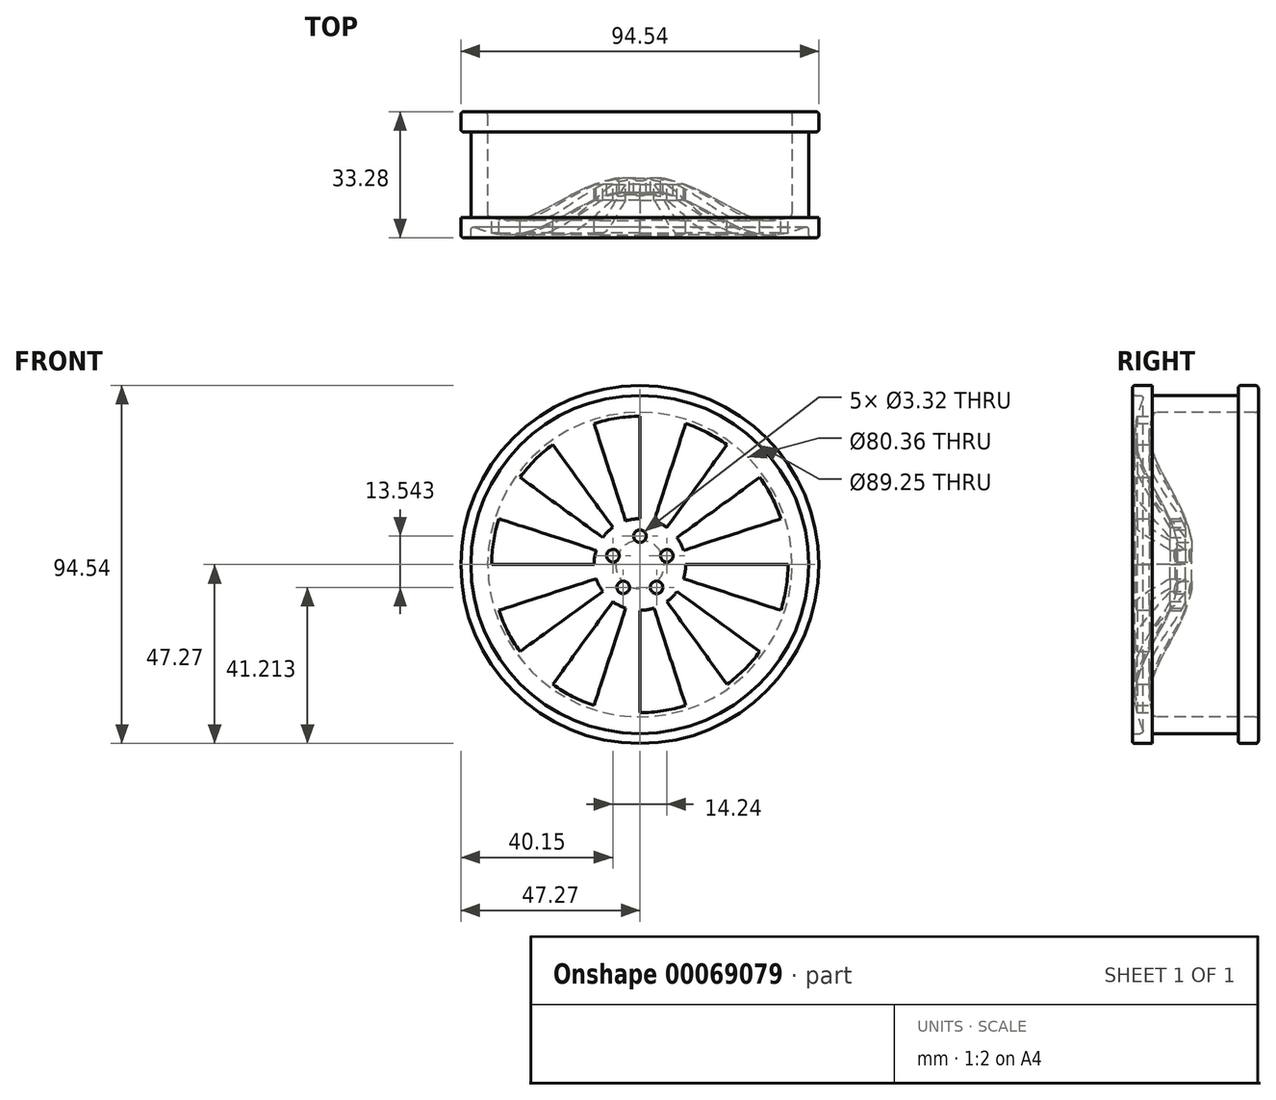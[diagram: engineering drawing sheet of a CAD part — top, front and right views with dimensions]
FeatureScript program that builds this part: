
annotation { "Feature Type Name" : "Feature", "Feature Type Description" : "" }
export const myFeature = defineFeature(function(context is Context, id is Id, definition is map)
    precondition{}
    {
        {
            var Q0;
            Q0=qCreatedBy(makeId("Top.planeOp"),FACE);
            var sketch = newSketch(context, id + "F0", { "sketchPlane" : qUnion([Q0])});
            skLineSegment(sketch, "E0.top", {"start": v(40.18, 30.1) * mm, "end": v(44.63, 30.1) * mm});
            skLineSegment(sketch, "E0.right", {"start": v(44.63, 2.16) * mm, "end": v(44.63, 27.94) * mm});
            skLineSegment(sketch, "E1.bottom", {"start": v(44.63, 30.1) * mm, "end": v(47.27, 30.1) * mm});
            skLineSegment(sketch, "E1.top", {"start": v(44.63, 0) * mm, "end": v(47.27, 0) * mm});
            skLineSegment(sketch, "E1.left", {"start": v(44.63, 27.94) * mm, "end": v(44.63, 2.16) * mm});
            skLineSegment(sketch, "E1.right", {"start": v(47.27, 30.1) * mm, "end": v(47.27, 27.94) * mm});
            skLineSegment(sketch, "E2.0", {"start": v(44.63, 2.16) * mm, "end": v(47.27, 2.16) * mm});
            skLineSegment(sketch, "E3.0", {"start": v(44.63, 27.94) * mm, "end": v(47.27, 27.94) * mm});
            skLineSegment(sketch, "E4.trimOffspring", {"start": v(47.27, 2.16) * mm, "end": v(47.27, 0) * mm});
            skLineSegment(sketch, "E5.0", {"start": v(40.18, 30.1) * mm, "end": v(40.18, 2.58) * mm});
            skLineSegment(sketch, "E6.bottom", {"start": v(0, 8.72) * mm, "end": v(6.4, 8.72) * mm});
            skLineSegment(sketch, "E6.top", {"start": v(0, 12.54) * mm, "end": v(6.4, 12.54) * mm});
            skLineSegment(sketch, "E6.left", {"start": v(0, 8.72) * mm, "end": v(0, 12.54) * mm});
            skPoint(sketch, "E7.1.internal.orphan", {"position": v(3.96, 8.72) * mm});
            skFitSpline(sketch, "E8", {"points": [v(6.4, 8.72) * mm, v(14.11, 5.82) * mm, v(31.92, -2.22) * mm, v(44.63, 0) * mm], "startDerivative": vector(25.8, -7.53) * mm, "endDerivative": vector(36.1, 13.86) * mm});
            skFitSpline(sketch, "E9", {"points": [v(6.4, 12.54) * mm, v(15.53, 9.4) * mm, v(32.03, 1.58) * mm, v(40.18, 2.58) * mm], "startDerivative": vector(27.2, -6.9) * mm, "endDerivative": vector(26.25, 9) * mm});
            skSolve(sketch);
        }
        {
            var Q0;
            Q0=makeQuery(id+"F0.imprint","IMPRINT",FACE,{"disambiguationData":[TD([[makeQuery(id+"F0.imprint","IMPRINT",EDGE,{"derivedFrom":sQuery(id+"F0.wireOp",EDGE,"E0.top")}),-1.0]])]});
            var Q1;
            Q1=sQuery(id+"F0.wireOp",EDGE,"E6.left");
            revolve(context, id + "F1", {"entities" : qUnion([Q0]), "axis" : qUnion([Q1]), "revolveType" : RevolveType.FULL});
        }
        {
            var Q0;
            Q0=makeQuery(id+"F1.opRevolve","SWEPT_FACE",FACE,{"disambiguationData":[OSD([sQuery(id+"F0.wireOp",EDGE,"E0.top"),sQuery(id+"F0.wireOp",EDGE,"E1.bottom")])]});
            var sketch = newSketch(context, id + "F2", { "sketchPlane" : qUnion([Q0])});
            skArc(sketch, "E10", {"start": v(-3.74, 11.52) * mm, "mid": v(-5.5, 10.79) * mm, "end": v(-7.12, 9.8) * mm});
            skLineSegment(sketch, "E11", {"start": v(-39.11, 0) * mm, "end": v(-12.1, 0) * mm});
            skLineSegment(sketch, "E12", {"start": v(0, 39.11) * mm, "end": v(0, 12.1) * mm});
            skLineSegment(sketch, "E13.1.0", {"start": v(-37.2, 12.09) * mm, "end": v(-11.52, 3.74) * mm});
            skLineSegment(sketch, "E13.1.1", {"start": v(-12.09, -37.2) * mm, "end": v(-3.74, -11.52) * mm});
            skLineSegment(sketch, "E13.2.0", {"start": v(-22.99, -31.64) * mm, "end": v(-7.12, -9.8) * mm});
            skLineSegment(sketch, "E13.2.1", {"start": v(31.64, -22.99) * mm, "end": v(9.8, -7.12) * mm});
            skLineSegment(sketch, "E13.3.0", {"start": v(22.99, -31.64) * mm, "end": v(7.12, -9.8) * mm});
            skLineSegment(sketch, "E13.3.1", {"start": v(31.64, 22.99) * mm, "end": v(9.8, 7.12) * mm});
            skLineSegment(sketch, "E13.4.0", {"start": v(37.2, 12.09) * mm, "end": v(11.52, 3.74) * mm});
            skLineSegment(sketch, "E13.4.1", {"start": v(-12.09, 37.2) * mm, "end": v(-3.74, 11.52) * mm});
            skArc(sketch, "E14", {"start": v(-12.09, 37.2) * mm, "mid": v(-17.76, 34.85) * mm, "end": v(-22.99, 31.64) * mm});
            skArc(sketch, "E15.trimOffspring", {"start": v(12.09, 37.2) * mm, "mid": v(6.12, 38.63) * mm, "end": v(0, 39.11) * mm});
            skArc(sketch, "E16.trimOffspring", {"start": v(31.64, 22.99) * mm, "mid": v(27.66, 27.66) * mm, "end": v(22.99, 31.64) * mm});
            skArc(sketch, "E17.trimOffspring", {"start": v(39.11, 0) * mm, "mid": v(38.63, 6.12) * mm, "end": v(37.2, 12.09) * mm});
            skArc(sketch, "E18.trimOffspring", {"start": v(31.64, -22.99) * mm, "mid": v(34.85, -17.76) * mm, "end": v(37.2, -12.09) * mm});
            skArc(sketch, "E19.trimOffspring", {"start": v(12.09, -37.2) * mm, "mid": v(17.76, -34.85) * mm, "end": v(22.99, -31.64) * mm});
            skArc(sketch, "E20.trimOffspring", {"start": v(-12.09, -37.2) * mm, "mid": v(-6.12, -38.63) * mm, "end": v(0, -39.11) * mm});
            skArc(sketch, "E21.trimOffspring", {"start": v(-31.64, -22.99) * mm, "mid": v(-27.66, -27.66) * mm, "end": v(-22.99, -31.64) * mm});
            skArc(sketch, "E22.trimOffspring", {"start": v(-39.11, 0) * mm, "mid": v(-38.63, -6.12) * mm, "end": v(-37.2, -12.09) * mm});
            skArc(sketch, "E23.trimOffspring", {"start": v(-31.64, 22.99) * mm, "mid": v(-34.85, 17.76) * mm, "end": v(-37.2, 12.09) * mm});
            skArc(sketch, "E24.trimOffspring", {"start": v(3.74, 11.52) * mm, "mid": v(1.9, 11.96) * mm, "end": v(0, 12.1) * mm});
            skArc(sketch, "E25.trimOffspring", {"start": v(9.8, 7.12) * mm, "mid": v(8.56, 8.56) * mm, "end": v(7.12, 9.8) * mm});
            skArc(sketch, "E26.trimOffspring", {"start": v(12.1, 0) * mm, "mid": v(11.96, 1.9) * mm, "end": v(11.52, 3.74) * mm});
            skArc(sketch, "E27.trimOffspring", {"start": v(9.8, -7.12) * mm, "mid": v(10.79, -5.5) * mm, "end": v(11.52, -3.74) * mm});
            skArc(sketch, "E28.trimOffspring", {"start": v(3.74, -11.52) * mm, "mid": v(5.5, -10.79) * mm, "end": v(7.12, -9.8) * mm});
            skArc(sketch, "E29.trimOffspring", {"start": v(-3.74, -11.52) * mm, "mid": v(-1.9, -11.96) * mm, "end": v(0, -12.1) * mm});
            skArc(sketch, "E30.trimOffspring", {"start": v(-9.8, -7.12) * mm, "mid": v(-8.56, -8.56) * mm, "end": v(-7.12, -9.8) * mm});
            skArc(sketch, "E31.trimOffspring", {"start": v(-12.1, 0) * mm, "mid": v(-11.96, -1.9) * mm, "end": v(-11.52, -3.74) * mm});
            skArc(sketch, "E32.trimOffspring", {"start": v(-9.8, 7.12) * mm, "mid": v(-10.79, 5.5) * mm, "end": v(-11.52, 3.74) * mm});
            skLineSegment(sketch, "E33.trimOffspring", {"start": v(11.52, -3.74) * mm, "end": v(37.2, -12.09) * mm});
            skLineSegment(sketch, "E34.trimOffspring", {"start": v(-9.8, 7.12) * mm, "end": v(-31.64, 22.99) * mm});
            skLineSegment(sketch, "E35.trimOffspring", {"start": v(-7.12, 9.8) * mm, "end": v(-22.99, 31.64) * mm});
            skLineSegment(sketch, "E36.trimOffspring", {"start": v(3.74, -11.52) * mm, "end": v(12.09, -37.2) * mm});
            skLineSegment(sketch, "E37.trimOffspring", {"start": v(0, -12.1) * mm, "end": v(0, -39.11) * mm});
            skLineSegment(sketch, "E38.trimOffspring", {"start": v(3.74, 11.52) * mm, "end": v(12.09, 37.2) * mm});
            skLineSegment(sketch, "E39.trimOffspring", {"start": v(7.12, 9.8) * mm, "end": v(22.99, 31.64) * mm});
            skLineSegment(sketch, "E40.trimOffspring", {"start": v(-9.8, -7.12) * mm, "end": v(-31.64, -22.99) * mm});
            skLineSegment(sketch, "E41.trimOffspring", {"start": v(-11.52, -3.74) * mm, "end": v(-37.2, -12.09) * mm});
            skLineSegment(sketch, "E42.trimOffspring", {"start": v(12.1, 0) * mm, "end": v(39.11, 0) * mm});
            skCircle(sketch, "E43", {"center": v(0, 7.49) * mm, "radius": 1.66 * mm});
            skCircle(sketch, "E44.1.0", {"center": v(-7.12, 2.31) * mm, "radius": 1.66 * mm});
            skCircle(sketch, "E44.2.0", {"center": v(-4.4, -6.06) * mm, "radius": 1.66 * mm});
            skCircle(sketch, "E44.3.0", {"center": v(4.4, -6.06) * mm, "radius": 1.66 * mm});
            skCircle(sketch, "E44.4.0", {"center": v(7.12, 2.31) * mm, "radius": 1.66 * mm});
            skPoint(sketch, "E45.orphan", {"position": v(-38.21, 12.42) * mm});
            skPoint(sketch, "E46.orphan", {"position": v(-32.5, 23.62) * mm});
            skPoint(sketch, "E47.orphan", {"position": v(-23.62, 32.5) * mm});
            skPoint(sketch, "E48.orphan", {"position": v(-40.18, 0) * mm});
            skPoint(sketch, "E49.orphan", {"position": v(-12.42, 38.21) * mm});
            skPoint(sketch, "E50.orphan", {"position": v(0, 40.18) * mm});
            skPoint(sketch, "E51.orphan", {"position": v(12.42, 38.21) * mm});
            skPoint(sketch, "E52.orphan", {"position": v(-38.21, -12.42) * mm});
            skPoint(sketch, "E53.orphan", {"position": v(23.62, 32.5) * mm});
            skPoint(sketch, "E54.orphan", {"position": v(32.5, 23.62) * mm});
            skPoint(sketch, "E55.orphan", {"position": v(38.21, 12.42) * mm});
            skPoint(sketch, "E56.orphan", {"position": v(40.18, 0) * mm});
            skPoint(sketch, "E57.orphan", {"position": v(-32.5, -23.62) * mm});
            skPoint(sketch, "E58.orphan", {"position": v(-23.62, -32.5) * mm});
            skPoint(sketch, "E59.orphan", {"position": v(-12.42, -38.21) * mm});
            skPoint(sketch, "E60.orphan", {"position": v(0, -40.18) * mm});
            skPoint(sketch, "E61.orphan", {"position": v(12.42, -38.21) * mm});
            skPoint(sketch, "E62.orphan", {"position": v(23.62, -32.5) * mm});
            skPoint(sketch, "E63.orphan", {"position": v(32.5, -23.62) * mm});
            skPoint(sketch, "E64.orphan", {"position": v(38.21, -12.42) * mm});
            skSolve(sketch);
        }
        {
            var Q0;
            Q0=makeQuery(id+"F2.imprint","IMPRINT",FACE,{"disambiguationData":[TD([[makeQuery(id+"F2.imprint","IMPRINT",EDGE,{"derivedFrom":sQuery(id+"F2.wireOp",EDGE,"E13.1.0")}),1.0]])]});
            var Q1;
            Q1=makeQuery(id+"F2.imprint","IMPRINT",FACE,{"disambiguationData":[TD([[makeQuery(id+"F2.imprint","IMPRINT",EDGE,{"derivedFrom":sQuery(id+"F2.wireOp",EDGE,"E10")}),-1.0]])]});
            var Q2;
            Q2=makeQuery(id+"F2.imprint","IMPRINT",FACE,{"disambiguationData":[TD([[makeQuery(id+"F2.imprint","IMPRINT",EDGE,{"derivedFrom":sQuery(id+"F2.wireOp",EDGE,"E12")}),1.0]])]});
            var Q3;
            Q3=makeQuery(id+"F2.imprint","IMPRINT",FACE,{"disambiguationData":[TD([[makeQuery(id+"F2.imprint","IMPRINT",EDGE,{"derivedFrom":sQuery(id+"F2.wireOp",EDGE,"E13.3.1")}),-1.0]])]});
            var Q4;
            Q4=makeQuery(id+"F2.imprint","IMPRINT",FACE,{"disambiguationData":[TD([[makeQuery(id+"F2.imprint","IMPRINT",EDGE,{"derivedFrom":sQuery(id+"F2.wireOp",EDGE,"E13.4.0")}),1.0]])]});
            var Q5;
            Q5=makeQuery(id+"F2.imprint","IMPRINT",FACE,{"disambiguationData":[TD([[makeQuery(id+"F2.imprint","IMPRINT",EDGE,{"derivedFrom":sQuery(id+"F2.wireOp",EDGE,"E13.2.1")}),-1.0]])]});
            var Q6;
            Q6=makeQuery(id+"F2.imprint","IMPRINT",FACE,{"disambiguationData":[TD([[makeQuery(id+"F2.imprint","IMPRINT",EDGE,{"derivedFrom":sQuery(id+"F2.wireOp",EDGE,"E13.3.0")}),1.0]])]});
            var Q7;
            Q7=makeQuery(id+"F2.imprint","IMPRINT",FACE,{"disambiguationData":[TD([[makeQuery(id+"F2.imprint","IMPRINT",EDGE,{"derivedFrom":sQuery(id+"F2.wireOp",EDGE,"E13.1.1")}),-1.0]])]});
            var Q8;
            Q8=makeQuery(id+"F2.imprint","IMPRINT",FACE,{"disambiguationData":[TD([[makeQuery(id+"F2.imprint","IMPRINT",EDGE,{"derivedFrom":sQuery(id+"F2.wireOp",EDGE,"E13.2.0")}),1.0]])]});
            var Q9;
            Q9=makeQuery(id+"F2.imprint","IMPRINT",FACE,{"disambiguationData":[TD([[makeQuery(id+"F2.imprint","IMPRINT",EDGE,{"derivedFrom":sQuery(id+"F2.wireOp",EDGE,"E11")}),-1.0]])]});
            var Q10;
            Q10=makeQuery(id+"F2.imprint","IMPRINT",FACE,{"disambiguationData":[TD([[makeQuery(id+"F2.imprint","IMPRINT",EDGE,{"derivedFrom":sQuery(id+"F2.wireOp",EDGE,"E44.1.0")}),1.0]])]});
            var Q11;
            Q11=makeQuery(id+"F2.imprint","IMPRINT",FACE,{"disambiguationData":[TD([[makeQuery(id+"F2.imprint","IMPRINT",EDGE,{"derivedFrom":sQuery(id+"F2.wireOp",EDGE,"E43")}),1.0]])]});
            var Q12;
            Q12=makeQuery(id+"F2.imprint","IMPRINT",FACE,{"disambiguationData":[TD([[makeQuery(id+"F2.imprint","IMPRINT",EDGE,{"derivedFrom":sQuery(id+"F2.wireOp",EDGE,"E44.4.0")}),1.0]])]});
            var Q13;
            Q13=makeQuery(id+"F2.imprint","IMPRINT",FACE,{"disambiguationData":[TD([[makeQuery(id+"F2.imprint","IMPRINT",EDGE,{"derivedFrom":sQuery(id+"F2.wireOp",EDGE,"E44.3.0")}),1.0]])]});
            var Q14;
            Q14=makeQuery(id+"F2.imprint","IMPRINT",FACE,{"disambiguationData":[TD([[makeQuery(id+"F2.imprint","IMPRINT",EDGE,{"derivedFrom":sQuery(id+"F2.wireOp",EDGE,"E44.2.0")}),1.0]])]});
            extrude(context, id + "F3", {"entities" : qUnion([Q0, Q1, Q2, Q3, Q4, Q5, Q6, Q7, Q8, Q9, Q10, Q11, Q12, Q13, Q14]), "operationType" : NewBodyOperationType.REMOVE, "endBound" : BoundingType.THROUGH_ALL, "oppositeDirection" : true, "depth" : 25.4 * mm});
        }
        {
            var Q0;
            Q0=makeQuery(id+"F1.opRevolve","SWEPT_FACE",FACE,{"disambiguationData":[OSD([sQuery(id+"F0.wireOp",EDGE,"E1.top")])]});
            extrude(context, id + "F4", {"entities" : qUnion([Q0]), "operationType" : NewBodyOperationType.ADD, "depth" : 3.17 * mm});
        }
        {
            var Q0;
            Q0=makeQuery(id+"F1.opRevolve","SWEPT_FACE",FACE,{"disambiguationData":[OSD([sQuery(id+"F0.wireOp",EDGE,"E3.0")])]});
            extrude(context, id + "F5", {"entities" : qUnion([Q0]), "operationType" : NewBodyOperationType.ADD, "depth" : 3.17 * mm});
        }
        {
            var Q0;
            Q0=makeQuery(id+"F4.opExtrude","CAP_EDGE",EDGE,{"disambiguationData":[OSD([sQuery(id+"F0.wireOp",EDGE,"E1.top"),sQuery(id+"F0.wireOp",EDGE,"b8091df5-9ebb-4b62-9d2d-79493e6e60fd.trimOffspring")])],"isStart":false});
            var Q1;
            {var subQ0=sQuery(id+"F0.wireOp",EDGE,"b8091df5-9ebb-4b62-9d2d-79493e6e60fd.trimOffspring");var subQ1=sQuery(id+"F0.wireOp",EDGE,"E1.top");Q1=makeQuery(id+"F4.boolean.opBoolean","MERGE",EDGE,{"derivedFrom":[makeQuery(id+"F1.opRevolve","SWEPT_EDGE",EDGE,{"disambiguationData":[OSD([subQ1,subQ0])]}),makeQuery(id+"F4.opExtrude","CAP_EDGE",EDGE,{"disambiguationData":[OSD([subQ1,subQ0])],"isStart":true})]});}
            var Q2;
            Q2=makeQuery(id+"F3.boolean.opBoolean","INTERSECT",EDGE,{"derivedFrom":[makeQuery(id+"F1.opRevolve","SWEPT_FACE",FACE,{"disambiguationData":[OSD([sQuery(id+"F0.wireOp",EDGE,"b8091df5-9ebb-4b62-9d2d-79493e6e60fd.trimOffspring")])]}),makeQuery(id+"F3.opExtrude","SWEPT_FACE",FACE,{"disambiguationData":[OSD([sQuery(id+"F2.wireOp",EDGE,"E19.trimOffspring")])]})]});
            var Q3;
            Q3=makeQuery(id+"F3.boolean.opBoolean","INTERSECT",EDGE,{"derivedFrom":[makeQuery(id+"F1.opRevolve","SWEPT_FACE",FACE,{"disambiguationData":[OSD([sQuery(id+"F0.wireOp",EDGE,"b8091df5-9ebb-4b62-9d2d-79493e6e60fd.trimOffspring")])]}),makeQuery(id+"F3.opExtrude","SWEPT_FACE",FACE,{"disambiguationData":[OSD([sQuery(id+"F2.wireOp",EDGE,"E20.trimOffspring")])]})]});
            var Q4;
            Q4=makeQuery(id+"F3.boolean.opBoolean","INTERSECT",EDGE,{"derivedFrom":[makeQuery(id+"F1.opRevolve","SWEPT_FACE",FACE,{"disambiguationData":[OSD([sQuery(id+"F0.wireOp",EDGE,"b8091df5-9ebb-4b62-9d2d-79493e6e60fd.trimOffspring")])]}),makeQuery(id+"F3.opExtrude","SWEPT_FACE",FACE,{"disambiguationData":[OSD([sQuery(id+"F2.wireOp",EDGE,"E21.trimOffspring")])]})]});
            var Q5;
            Q5=makeQuery(id+"F3.boolean.opBoolean","INTERSECT",EDGE,{"derivedFrom":[makeQuery(id+"F1.opRevolve","SWEPT_FACE",FACE,{"disambiguationData":[OSD([sQuery(id+"F0.wireOp",EDGE,"b8091df5-9ebb-4b62-9d2d-79493e6e60fd.trimOffspring")])]}),makeQuery(id+"F3.opExtrude","SWEPT_FACE",FACE,{"disambiguationData":[OSD([sQuery(id+"F2.wireOp",EDGE,"E22.trimOffspring")])]})]});
            var Q6;
            Q6=makeQuery(id+"F3.boolean.opBoolean","INTERSECT",EDGE,{"derivedFrom":[makeQuery(id+"F1.opRevolve","SWEPT_FACE",FACE,{"disambiguationData":[OSD([sQuery(id+"F0.wireOp",EDGE,"b8091df5-9ebb-4b62-9d2d-79493e6e60fd.trimOffspring")])]}),makeQuery(id+"F3.opExtrude","SWEPT_FACE",FACE,{"disambiguationData":[OSD([sQuery(id+"F2.wireOp",EDGE,"E23.trimOffspring")])]})]});
            var Q7;
            Q7=makeQuery(id+"F3.boolean.opBoolean","INTERSECT",EDGE,{"derivedFrom":[makeQuery(id+"F1.opRevolve","SWEPT_FACE",FACE,{"disambiguationData":[OSD([sQuery(id+"F0.wireOp",EDGE,"b8091df5-9ebb-4b62-9d2d-79493e6e60fd.trimOffspring")])]}),makeQuery(id+"F3.opExtrude","SWEPT_FACE",FACE,{"disambiguationData":[OSD([sQuery(id+"F2.wireOp",EDGE,"E14")])]})]});
            var Q8;
            Q8=makeQuery(id+"F3.boolean.opBoolean","INTERSECT",EDGE,{"derivedFrom":[makeQuery(id+"F1.opRevolve","SWEPT_FACE",FACE,{"disambiguationData":[OSD([sQuery(id+"F0.wireOp",EDGE,"b8091df5-9ebb-4b62-9d2d-79493e6e60fd.trimOffspring")])]}),makeQuery(id+"F3.opExtrude","SWEPT_FACE",FACE,{"disambiguationData":[OSD([sQuery(id+"F2.wireOp",EDGE,"E15.trimOffspring")])]})]});
            var Q9;
            Q9=makeQuery(id+"F3.boolean.opBoolean","INTERSECT",EDGE,{"derivedFrom":[makeQuery(id+"F1.opRevolve","SWEPT_FACE",FACE,{"disambiguationData":[OSD([sQuery(id+"F0.wireOp",EDGE,"b8091df5-9ebb-4b62-9d2d-79493e6e60fd.trimOffspring")])]}),makeQuery(id+"F3.opExtrude","SWEPT_FACE",FACE,{"disambiguationData":[OSD([sQuery(id+"F2.wireOp",EDGE,"E16.trimOffspring")])]})]});
            var Q10;
            Q10=makeQuery(id+"F3.boolean.opBoolean","INTERSECT",EDGE,{"derivedFrom":[makeQuery(id+"F1.opRevolve","SWEPT_FACE",FACE,{"disambiguationData":[OSD([sQuery(id+"F0.wireOp",EDGE,"b8091df5-9ebb-4b62-9d2d-79493e6e60fd.trimOffspring")])]}),makeQuery(id+"F3.opExtrude","SWEPT_FACE",FACE,{"disambiguationData":[OSD([sQuery(id+"F2.wireOp",EDGE,"E17.trimOffspring")])]})]});
            var Q11;
            Q11=makeQuery(id+"F3.boolean.opBoolean","INTERSECT",EDGE,{"derivedFrom":[makeQuery(id+"F1.opRevolve","SWEPT_FACE",FACE,{"disambiguationData":[OSD([sQuery(id+"F0.wireOp",EDGE,"b8091df5-9ebb-4b62-9d2d-79493e6e60fd.trimOffspring")])]}),makeQuery(id+"F3.opExtrude","SWEPT_FACE",FACE,{"disambiguationData":[OSD([sQuery(id+"F2.wireOp",EDGE,"E18.trimOffspring")])]})]});
            var Q12;
            Q12=makeQuery(id+"F3.boolean.opBoolean","INTERSECT",EDGE,{"derivedFrom":[makeQuery(id+"F1.opRevolve","SWEPT_FACE",FACE,{"disambiguationData":[OSD([sQuery(id+"F0.wireOp",EDGE,"b8091df5-9ebb-4b62-9d2d-79493e6e60fd.trimOffspring")])]}),makeQuery(id+"F3.opExtrude","SWEPT_FACE",FACE,{"disambiguationData":[OSD([sQuery(id+"F2.wireOp",EDGE,"E33.trimOffspring")])]})]});
            var Q13;
            Q13=makeQuery(id+"F3.boolean.opBoolean","INTERSECT",EDGE,{"derivedFrom":[makeQuery(id+"F1.opRevolve","SWEPT_FACE",FACE,{"disambiguationData":[OSD([sQuery(id+"F0.wireOp",EDGE,"b8091df5-9ebb-4b62-9d2d-79493e6e60fd.trimOffspring")])]}),makeQuery(id+"F3.opExtrude","SWEPT_FACE",FACE,{"disambiguationData":[OSD([sQuery(id+"F2.wireOp",EDGE,"E13.2.1")])]})]});
            var Q14;
            Q14=makeQuery(id+"F3.boolean.opBoolean","INTERSECT",EDGE,{"derivedFrom":[makeQuery(id+"F1.opRevolve","SWEPT_FACE",FACE,{"disambiguationData":[OSD([sQuery(id+"F0.wireOp",EDGE,"b8091df5-9ebb-4b62-9d2d-79493e6e60fd.trimOffspring")])]}),makeQuery(id+"F3.opExtrude","SWEPT_FACE",FACE,{"disambiguationData":[OSD([sQuery(id+"F2.wireOp",EDGE,"E27.trimOffspring")])]})]});
            var Q15;
            Q15=makeQuery(id+"F3.boolean.opBoolean","INTERSECT",EDGE,{"derivedFrom":[makeQuery(id+"F1.opRevolve","SWEPT_FACE",FACE,{"disambiguationData":[OSD([sQuery(id+"F0.wireOp",EDGE,"b8091df5-9ebb-4b62-9d2d-79493e6e60fd.trimOffspring")])]}),makeQuery(id+"F3.opExtrude","SWEPT_FACE",FACE,{"disambiguationData":[OSD([sQuery(id+"F2.wireOp",EDGE,"E13.3.0")])]})]});
            var Q16;
            Q16=makeQuery(id+"F3.boolean.opBoolean","INTERSECT",EDGE,{"derivedFrom":[makeQuery(id+"F1.opRevolve","SWEPT_FACE",FACE,{"disambiguationData":[OSD([sQuery(id+"F0.wireOp",EDGE,"b8091df5-9ebb-4b62-9d2d-79493e6e60fd.trimOffspring")])]}),makeQuery(id+"F3.opExtrude","SWEPT_FACE",FACE,{"disambiguationData":[OSD([sQuery(id+"F2.wireOp",EDGE,"E36.trimOffspring")])]})]});
            var Q17;
            Q17=makeQuery(id+"F3.boolean.opBoolean","INTERSECT",EDGE,{"derivedFrom":[makeQuery(id+"F1.opRevolve","SWEPT_FACE",FACE,{"disambiguationData":[OSD([sQuery(id+"F0.wireOp",EDGE,"b8091df5-9ebb-4b62-9d2d-79493e6e60fd.trimOffspring")])]}),makeQuery(id+"F3.opExtrude","SWEPT_FACE",FACE,{"disambiguationData":[OSD([sQuery(id+"F2.wireOp",EDGE,"E28.trimOffspring")])]})]});
            var Q18;
            Q18=makeQuery(id+"F3.boolean.opBoolean","INTERSECT",EDGE,{"derivedFrom":[makeQuery(id+"F1.opRevolve","SWEPT_FACE",FACE,{"disambiguationData":[OSD([sQuery(id+"F0.wireOp",EDGE,"b8091df5-9ebb-4b62-9d2d-79493e6e60fd.trimOffspring")])]}),makeQuery(id+"F3.opExtrude","SWEPT_FACE",FACE,{"disambiguationData":[OSD([sQuery(id+"F2.wireOp",EDGE,"E29.trimOffspring")])]})]});
            var Q19;
            Q19=makeQuery(id+"F3.boolean.opBoolean","INTERSECT",EDGE,{"derivedFrom":[makeQuery(id+"F1.opRevolve","SWEPT_FACE",FACE,{"disambiguationData":[OSD([sQuery(id+"F0.wireOp",EDGE,"b8091df5-9ebb-4b62-9d2d-79493e6e60fd.trimOffspring")])]}),makeQuery(id+"F3.opExtrude","SWEPT_FACE",FACE,{"disambiguationData":[OSD([sQuery(id+"F2.wireOp",EDGE,"E37.trimOffspring")])]})]});
            var Q20;
            Q20=makeQuery(id+"F3.boolean.opBoolean","INTERSECT",EDGE,{"derivedFrom":[makeQuery(id+"F1.opRevolve","SWEPT_FACE",FACE,{"disambiguationData":[OSD([sQuery(id+"F0.wireOp",EDGE,"b8091df5-9ebb-4b62-9d2d-79493e6e60fd.trimOffspring")])]}),makeQuery(id+"F3.opExtrude","SWEPT_FACE",FACE,{"disambiguationData":[OSD([sQuery(id+"F2.wireOp",EDGE,"E13.1.1")])]})]});
            var Q21;
            Q21=makeQuery(id+"F3.boolean.opBoolean","INTERSECT",EDGE,{"derivedFrom":[makeQuery(id+"F1.opRevolve","SWEPT_FACE",FACE,{"disambiguationData":[OSD([sQuery(id+"F0.wireOp",EDGE,"b8091df5-9ebb-4b62-9d2d-79493e6e60fd.trimOffspring")])]}),makeQuery(id+"F3.opExtrude","SWEPT_FACE",FACE,{"disambiguationData":[OSD([sQuery(id+"F2.wireOp",EDGE,"E13.2.0")])]})]});
            var Q22;
            Q22=makeQuery(id+"F3.boolean.opBoolean","INTERSECT",EDGE,{"derivedFrom":[makeQuery(id+"F1.opRevolve","SWEPT_FACE",FACE,{"disambiguationData":[OSD([sQuery(id+"F0.wireOp",EDGE,"b8091df5-9ebb-4b62-9d2d-79493e6e60fd.trimOffspring")])]}),makeQuery(id+"F3.opExtrude","SWEPT_FACE",FACE,{"disambiguationData":[OSD([sQuery(id+"F2.wireOp",EDGE,"E40.trimOffspring")])]})]});
            var Q23;
            Q23=makeQuery(id+"F3.boolean.opBoolean","INTERSECT",EDGE,{"derivedFrom":[makeQuery(id+"F1.opRevolve","SWEPT_FACE",FACE,{"disambiguationData":[OSD([sQuery(id+"F0.wireOp",EDGE,"b8091df5-9ebb-4b62-9d2d-79493e6e60fd.trimOffspring")])]}),makeQuery(id+"F3.opExtrude","SWEPT_FACE",FACE,{"disambiguationData":[OSD([sQuery(id+"F2.wireOp",EDGE,"E30.trimOffspring")])]})]});
            var Q24;
            Q24=makeQuery(id+"F3.boolean.opBoolean","INTERSECT",EDGE,{"derivedFrom":[makeQuery(id+"F1.opRevolve","SWEPT_FACE",FACE,{"disambiguationData":[OSD([sQuery(id+"F0.wireOp",EDGE,"b8091df5-9ebb-4b62-9d2d-79493e6e60fd.trimOffspring")])]}),makeQuery(id+"F3.opExtrude","SWEPT_FACE",FACE,{"disambiguationData":[OSD([sQuery(id+"F2.wireOp",EDGE,"E11")])]})]});
            var Q25;
            Q25=makeQuery(id+"F3.boolean.opBoolean","INTERSECT",EDGE,{"derivedFrom":[makeQuery(id+"F1.opRevolve","SWEPT_FACE",FACE,{"disambiguationData":[OSD([sQuery(id+"F0.wireOp",EDGE,"b8091df5-9ebb-4b62-9d2d-79493e6e60fd.trimOffspring")])]}),makeQuery(id+"F3.opExtrude","SWEPT_FACE",FACE,{"disambiguationData":[OSD([sQuery(id+"F2.wireOp",EDGE,"E41.trimOffspring")])]})]});
            var Q26;
            Q26=makeQuery(id+"F3.boolean.opBoolean","INTERSECT",EDGE,{"derivedFrom":[makeQuery(id+"F1.opRevolve","SWEPT_FACE",FACE,{"disambiguationData":[OSD([sQuery(id+"F0.wireOp",EDGE,"b8091df5-9ebb-4b62-9d2d-79493e6e60fd.trimOffspring")])]}),makeQuery(id+"F3.opExtrude","SWEPT_FACE",FACE,{"disambiguationData":[OSD([sQuery(id+"F2.wireOp",EDGE,"E31.trimOffspring")])]})]});
            var Q27;
            Q27=makeQuery(id+"F3.boolean.opBoolean","INTERSECT",EDGE,{"derivedFrom":[makeQuery(id+"F1.opRevolve","SWEPT_FACE",FACE,{"disambiguationData":[OSD([sQuery(id+"F0.wireOp",EDGE,"b8091df5-9ebb-4b62-9d2d-79493e6e60fd.trimOffspring")])]}),makeQuery(id+"F3.opExtrude","SWEPT_FACE",FACE,{"disambiguationData":[OSD([sQuery(id+"F2.wireOp",EDGE,"E13.1.0")])]})]});
            var Q28;
            Q28=makeQuery(id+"F3.boolean.opBoolean","INTERSECT",EDGE,{"derivedFrom":[makeQuery(id+"F1.opRevolve","SWEPT_FACE",FACE,{"disambiguationData":[OSD([sQuery(id+"F0.wireOp",EDGE,"b8091df5-9ebb-4b62-9d2d-79493e6e60fd.trimOffspring")])]}),makeQuery(id+"F3.opExtrude","SWEPT_FACE",FACE,{"disambiguationData":[OSD([sQuery(id+"F2.wireOp",EDGE,"E32.trimOffspring")])]})]});
            var Q29;
            Q29=makeQuery(id+"F3.boolean.opBoolean","INTERSECT",EDGE,{"derivedFrom":[makeQuery(id+"F1.opRevolve","SWEPT_FACE",FACE,{"disambiguationData":[OSD([sQuery(id+"F0.wireOp",EDGE,"b8091df5-9ebb-4b62-9d2d-79493e6e60fd.trimOffspring")])]}),makeQuery(id+"F3.opExtrude","SWEPT_FACE",FACE,{"disambiguationData":[OSD([sQuery(id+"F2.wireOp",EDGE,"E34.trimOffspring")])]})]});
            var Q30;
            Q30=makeQuery(id+"F3.boolean.opBoolean","INTERSECT",EDGE,{"derivedFrom":[makeQuery(id+"F1.opRevolve","SWEPT_FACE",FACE,{"disambiguationData":[OSD([sQuery(id+"F0.wireOp",EDGE,"b8091df5-9ebb-4b62-9d2d-79493e6e60fd.trimOffspring")])]}),makeQuery(id+"F3.opExtrude","SWEPT_FACE",FACE,{"disambiguationData":[OSD([sQuery(id+"F2.wireOp",EDGE,"E13.4.1")])]})]});
            var Q31;
            Q31=makeQuery(id+"F3.boolean.opBoolean","INTERSECT",EDGE,{"derivedFrom":[makeQuery(id+"F1.opRevolve","SWEPT_FACE",FACE,{"disambiguationData":[OSD([sQuery(id+"F0.wireOp",EDGE,"b8091df5-9ebb-4b62-9d2d-79493e6e60fd.trimOffspring")])]}),makeQuery(id+"F3.opExtrude","SWEPT_FACE",FACE,{"disambiguationData":[OSD([sQuery(id+"F2.wireOp",EDGE,"E35.trimOffspring")])]})]});
            var Q32;
            Q32=makeQuery(id+"F3.boolean.opBoolean","INTERSECT",EDGE,{"derivedFrom":[makeQuery(id+"F1.opRevolve","SWEPT_FACE",FACE,{"disambiguationData":[OSD([sQuery(id+"F0.wireOp",EDGE,"b8091df5-9ebb-4b62-9d2d-79493e6e60fd.trimOffspring")])]}),makeQuery(id+"F3.opExtrude","SWEPT_FACE",FACE,{"disambiguationData":[OSD([sQuery(id+"F2.wireOp",EDGE,"E10")])]})]});
            var Q33;
            Q33=makeQuery(id+"F3.boolean.opBoolean","INTERSECT",EDGE,{"derivedFrom":[makeQuery(id+"F1.opRevolve","SWEPT_FACE",FACE,{"disambiguationData":[OSD([sQuery(id+"F0.wireOp",EDGE,"b8091df5-9ebb-4b62-9d2d-79493e6e60fd.trimOffspring")])]}),makeQuery(id+"F3.opExtrude","SWEPT_FACE",FACE,{"disambiguationData":[OSD([sQuery(id+"F2.wireOp",EDGE,"E38.trimOffspring")])]})]});
            var Q34;
            Q34=makeQuery(id+"F3.boolean.opBoolean","INTERSECT",EDGE,{"derivedFrom":[makeQuery(id+"F1.opRevolve","SWEPT_FACE",FACE,{"disambiguationData":[OSD([sQuery(id+"F0.wireOp",EDGE,"b8091df5-9ebb-4b62-9d2d-79493e6e60fd.trimOffspring")])]}),makeQuery(id+"F3.opExtrude","SWEPT_FACE",FACE,{"disambiguationData":[OSD([sQuery(id+"F2.wireOp",EDGE,"E12")])]})]});
            var Q35;
            Q35=makeQuery(id+"F3.boolean.opBoolean","INTERSECT",EDGE,{"derivedFrom":[makeQuery(id+"F1.opRevolve","SWEPT_FACE",FACE,{"disambiguationData":[OSD([sQuery(id+"F0.wireOp",EDGE,"b8091df5-9ebb-4b62-9d2d-79493e6e60fd.trimOffspring")])]}),makeQuery(id+"F3.opExtrude","SWEPT_FACE",FACE,{"disambiguationData":[OSD([sQuery(id+"F2.wireOp",EDGE,"E24.trimOffspring")])]})]});
            var Q36;
            Q36=makeQuery(id+"F3.boolean.opBoolean","INTERSECT",EDGE,{"derivedFrom":[makeQuery(id+"F1.opRevolve","SWEPT_FACE",FACE,{"disambiguationData":[OSD([sQuery(id+"F0.wireOp",EDGE,"b8091df5-9ebb-4b62-9d2d-79493e6e60fd.trimOffspring")])]}),makeQuery(id+"F3.opExtrude","SWEPT_FACE",FACE,{"disambiguationData":[OSD([sQuery(id+"F2.wireOp",EDGE,"E13.3.1")])]})]});
            var Q37;
            Q37=makeQuery(id+"F3.boolean.opBoolean","INTERSECT",EDGE,{"derivedFrom":[makeQuery(id+"F1.opRevolve","SWEPT_FACE",FACE,{"disambiguationData":[OSD([sQuery(id+"F0.wireOp",EDGE,"b8091df5-9ebb-4b62-9d2d-79493e6e60fd.trimOffspring")])]}),makeQuery(id+"F3.opExtrude","SWEPT_FACE",FACE,{"disambiguationData":[OSD([sQuery(id+"F2.wireOp",EDGE,"E39.trimOffspring")])]})]});
            var Q38;
            Q38=makeQuery(id+"F3.boolean.opBoolean","INTERSECT",EDGE,{"derivedFrom":[makeQuery(id+"F1.opRevolve","SWEPT_FACE",FACE,{"disambiguationData":[OSD([sQuery(id+"F0.wireOp",EDGE,"b8091df5-9ebb-4b62-9d2d-79493e6e60fd.trimOffspring")])]}),makeQuery(id+"F3.opExtrude","SWEPT_FACE",FACE,{"disambiguationData":[OSD([sQuery(id+"F2.wireOp",EDGE,"E25.trimOffspring")])]})]});
            var Q39;
            Q39=makeQuery(id+"F3.boolean.opBoolean","INTERSECT",EDGE,{"derivedFrom":[makeQuery(id+"F1.opRevolve","SWEPT_FACE",FACE,{"disambiguationData":[OSD([sQuery(id+"F0.wireOp",EDGE,"b8091df5-9ebb-4b62-9d2d-79493e6e60fd.trimOffspring")])]}),makeQuery(id+"F3.opExtrude","SWEPT_FACE",FACE,{"disambiguationData":[OSD([sQuery(id+"F2.wireOp",EDGE,"E26.trimOffspring")])]})]});
            var Q40;
            Q40=makeQuery(id+"F3.boolean.opBoolean","INTERSECT",EDGE,{"derivedFrom":[makeQuery(id+"F1.opRevolve","SWEPT_FACE",FACE,{"disambiguationData":[OSD([sQuery(id+"F0.wireOp",EDGE,"b8091df5-9ebb-4b62-9d2d-79493e6e60fd.trimOffspring")])]}),makeQuery(id+"F3.opExtrude","SWEPT_FACE",FACE,{"disambiguationData":[OSD([sQuery(id+"F2.wireOp",EDGE,"E13.4.0")])]})]});
            var Q41;
            Q41=makeQuery(id+"F3.boolean.opBoolean","INTERSECT",EDGE,{"derivedFrom":[makeQuery(id+"F1.opRevolve","SWEPT_FACE",FACE,{"disambiguationData":[OSD([sQuery(id+"F0.wireOp",EDGE,"b8091df5-9ebb-4b62-9d2d-79493e6e60fd.trimOffspring")])]}),makeQuery(id+"F3.opExtrude","SWEPT_FACE",FACE,{"disambiguationData":[OSD([sQuery(id+"F2.wireOp",EDGE,"E42.trimOffspring")])]})]});
            var Q42;
            {var subQ0=sQuery(id+"F0.wireOp",EDGE,"E6.bottom");var subQ1=sQuery(id+"F0.wireOp",EDGE,"b8091df5-9ebb-4b62-9d2d-79493e6e60fd.trimOffspring");Q42=makeQuery(id+"F3.boolean.opBoolean","SPLIT",EDGE,{"disambiguationData":[TD([makeQuery(id+"F1.opRevolve","SWEPT_FACE",FACE,{"disambiguationData":[OSD([subQ0])]}),makeQuery(id+"F1.opRevolve","SWEPT_FACE",FACE,{"disambiguationData":[OSD([subQ1])]}),makeQuery(id+"F3.opExtrude","SWEPT_FACE",FACE,{"disambiguationData":[OSD([sQuery(id+"F2.wireOp",EDGE,"E43")])]}),makeQuery(id+"F3.opExtrude","SWEPT_FACE",FACE,{"disambiguationData":[OSD([sQuery(id+"F2.wireOp",EDGE,"E44.4.0")])]})])],"derivedFrom":makeQuery(id+"F1.opRevolve","SWEPT_EDGE",EDGE,{"disambiguationData":[OSD([subQ0,subQ1])]})});}
            var Q43;
            {var subQ0=sQuery(id+"F0.wireOp",EDGE,"E6.bottom");var subQ1=sQuery(id+"F0.wireOp",EDGE,"b8091df5-9ebb-4b62-9d2d-79493e6e60fd.trimOffspring");Q43=makeQuery(id+"F3.boolean.opBoolean","SPLIT",EDGE,{"disambiguationData":[TD([makeQuery(id+"F1.opRevolve","SWEPT_FACE",FACE,{"disambiguationData":[OSD([subQ0])]}),makeQuery(id+"F1.opRevolve","SWEPT_FACE",FACE,{"disambiguationData":[OSD([subQ1])]}),makeQuery(id+"F3.opExtrude","SWEPT_FACE",FACE,{"disambiguationData":[OSD([sQuery(id+"F2.wireOp",EDGE,"E43")])]}),makeQuery(id+"F3.opExtrude","SWEPT_FACE",FACE,{"disambiguationData":[OSD([sQuery(id+"F2.wireOp",EDGE,"E44.1.0")])]})])],"derivedFrom":makeQuery(id+"F1.opRevolve","SWEPT_EDGE",EDGE,{"disambiguationData":[OSD([subQ0,subQ1])]})});}
            var Q44;
            {var subQ0=sQuery(id+"F0.wireOp",EDGE,"E6.bottom");var subQ1=sQuery(id+"F0.wireOp",EDGE,"b8091df5-9ebb-4b62-9d2d-79493e6e60fd.trimOffspring");Q44=makeQuery(id+"F3.boolean.opBoolean","SPLIT",EDGE,{"disambiguationData":[TD([makeQuery(id+"F1.opRevolve","SWEPT_FACE",FACE,{"disambiguationData":[OSD([subQ0])]}),makeQuery(id+"F1.opRevolve","SWEPT_FACE",FACE,{"disambiguationData":[OSD([subQ1])]}),makeQuery(id+"F3.opExtrude","SWEPT_FACE",FACE,{"disambiguationData":[OSD([sQuery(id+"F2.wireOp",EDGE,"E44.3.0")])]}),makeQuery(id+"F3.opExtrude","SWEPT_FACE",FACE,{"disambiguationData":[OSD([sQuery(id+"F2.wireOp",EDGE,"E44.4.0")])]})])],"derivedFrom":makeQuery(id+"F1.opRevolve","SWEPT_EDGE",EDGE,{"disambiguationData":[OSD([subQ0,subQ1])]})});}
            var Q45;
            {var subQ0=sQuery(id+"F0.wireOp",EDGE,"E6.bottom");var subQ1=sQuery(id+"F0.wireOp",EDGE,"b8091df5-9ebb-4b62-9d2d-79493e6e60fd.trimOffspring");Q45=makeQuery(id+"F3.boolean.opBoolean","SPLIT",EDGE,{"disambiguationData":[TD([makeQuery(id+"F1.opRevolve","SWEPT_FACE",FACE,{"disambiguationData":[OSD([subQ0])]}),makeQuery(id+"F1.opRevolve","SWEPT_FACE",FACE,{"disambiguationData":[OSD([subQ1])]}),makeQuery(id+"F3.opExtrude","SWEPT_FACE",FACE,{"disambiguationData":[OSD([sQuery(id+"F2.wireOp",EDGE,"E44.2.0")])]}),makeQuery(id+"F3.opExtrude","SWEPT_FACE",FACE,{"disambiguationData":[OSD([sQuery(id+"F2.wireOp",EDGE,"E44.3.0")])]})])],"derivedFrom":makeQuery(id+"F1.opRevolve","SWEPT_EDGE",EDGE,{"disambiguationData":[OSD([subQ0,subQ1])]})});}
            var Q46;
            {var subQ0=sQuery(id+"F0.wireOp",EDGE,"E6.bottom");var subQ1=sQuery(id+"F0.wireOp",EDGE,"b8091df5-9ebb-4b62-9d2d-79493e6e60fd.trimOffspring");Q46=makeQuery(id+"F3.boolean.opBoolean","SPLIT",EDGE,{"disambiguationData":[TD([makeQuery(id+"F1.opRevolve","SWEPT_FACE",FACE,{"disambiguationData":[OSD([subQ0])]}),makeQuery(id+"F1.opRevolve","SWEPT_FACE",FACE,{"disambiguationData":[OSD([subQ1])]}),makeQuery(id+"F3.opExtrude","SWEPT_FACE",FACE,{"disambiguationData":[OSD([sQuery(id+"F2.wireOp",EDGE,"E44.1.0")])]}),makeQuery(id+"F3.opExtrude","SWEPT_FACE",FACE,{"disambiguationData":[OSD([sQuery(id+"F2.wireOp",EDGE,"E44.2.0")])]})])],"derivedFrom":makeQuery(id+"F1.opRevolve","SWEPT_EDGE",EDGE,{"disambiguationData":[OSD([subQ0,subQ1])]})});}
            fillet(context, id + "F6", {"entities" : qUnion([Q0, Q1, Q2, Q3, Q4, Q5, Q6, Q7, Q8, Q9, Q10, Q11, Q12, Q13, Q14, Q15, Q16, Q17, Q18, Q19, Q20, Q21, Q22, Q23, Q24, Q25, Q26, Q27, Q28, Q29, Q30, Q31, Q32, Q33, Q34, Q35, Q36, Q37, Q38, Q39, Q40, Q41, Q42, Q43, Q44, Q45, Q46]), "radius" : 0.76 * mm, "tangentPropagation" : true, "allowEdgeOverflow" : false});
        }
        {
            var Q0;
            Q0=makeQuery(id+"F4.opExtrude","CAP_EDGE",EDGE,{"disambiguationData":[OSD([sQuery(id+"F0.wireOp",EDGE,"E1.top"),sQuery(id+"F0.wireOp",EDGE,"E4.trimOffspring")])],"isStart":false});
            var Q1;
            Q1=makeQuery(id+"F1.opRevolve","SWEPT_EDGE",EDGE,{"disambiguationData":[OSD([sQuery(id+"F0.wireOp",EDGE,"E1.bottom"),sQuery(id+"F0.wireOp",EDGE,"E1.right")])]});
            var Q2;
            Q2=makeQuery(id+"F5.opExtrude","CAP_EDGE",EDGE,{"disambiguationData":[OSD([sQuery(id+"F0.wireOp",EDGE,"E1.left"),sQuery(id+"F0.wireOp",EDGE,"E3.0")])],"isStart":false});
            var Q3;
            Q3=makeQuery(id+"F1.opRevolve","SWEPT_FACE",FACE,{"disambiguationData":[OSD([sQuery(id+"F0.wireOp",EDGE,"E1.left")])]});
            var Q4;
            Q4=makeQuery(id+"F1.opRevolve","SWEPT_EDGE",EDGE,{"disambiguationData":[OSD([sQuery(id+"F0.wireOp",EDGE,"c0b38bb9-df9c-4255-b039-9b41b91256a7.0"),sQuery(id+"F0.wireOp",EDGE,"E5.0")])]});
            var Q5;
            Q5=makeQuery(id+"F1.opRevolve","SWEPT_EDGE",EDGE,{"disambiguationData":[OSD([sQuery(id+"F0.wireOp",EDGE,"E0.top"),sQuery(id+"F0.wireOp",EDGE,"E5.0")])]});
            fillet(context, id + "F7", {"entities" : qUnion([Q0, Q1, Q2, Q3, Q4, Q5]), "radius" : 0.76 * mm, "tangentPropagation" : true, "allowEdgeOverflow" : false});
        }
        {
            var Q0;
            Q0=makeQuery(id+"F1.opRevolve","SWEPT_FACE",FACE,{"disambiguationData":[OSD([sQuery(id+"F0.wireOp",EDGE,"E6.bottom")])]});
            var sketch = newSketch(context, id + "F8", { "sketchPlane" : qUnion([Q0])});
            skCircle(sketch, "E65", {"center": v(0, 0) * mm, "radius": 4.45 * mm});
            skSolve(sketch);
        }
        {
            var Q0;
            Q0=makeQuery(id+"F8.imprint","IMPRINT",FACE,{"disambiguationData":[TD([[makeQuery(id+"F8.imprint","IMPRINT",EDGE,{"derivedFrom":sQuery(id+"F8.wireOp",EDGE,"E65")}),1.0]])]});
            extrude(context, id + "F9", {"entities" : qUnion([Q0]), "operationType" : NewBodyOperationType.ADD, "depth" : 0.5 * mm});
        }
        {
            var Q0;
            Q0=makeQuery(id+"F9.opExtrude","CAP_EDGE",EDGE,{"disambiguationData":[OSD([sQuery(id+"F8.wireOp",EDGE,"E65")])],"isStart":false});
            chamfer(context, id + "F10", {"entities" : qUnion([Q0]), "width" : 0.5 * mm, "tangentPropagation" : true});
        }
        {
            var Q0;
            {var subQ0=sQuery(id+"F8.wireOp",EDGE,"E65");Q0=makeQuery(id+"F10.opChamfer","BLEND_EDGE",EDGE,{"blendedFrom":[makeQuery(id+"F9.opExtrude","CAP_EDGE",EDGE,{"disambiguationData":[OSD([subQ0])],"isStart":false}),makeQuery(id+"F9.opExtrude","CAP_FACE",FACE,{"disambiguationData":[OSD([subQ0])],"isStart":false})],"blendedInto":[makeQuery(id+"F9.opExtrude","CAP_FACE",FACE,{"disambiguationData":[OSD([subQ0])],"isStart":false})]});}
            var Q1;
            Q1=makeQuery(id+"F10.opChamfer","BLEND_EDGE",EDGE,{"blendedFrom":[makeQuery(id+"F9.opExtrude","CAP_EDGE",EDGE,{"disambiguationData":[OSD([sQuery(id+"F8.wireOp",EDGE,"E65")])],"isStart":false}),makeQuery(id+"F1.opRevolve","SWEPT_FACE",FACE,{"disambiguationData":[OSD([sQuery(id+"F0.wireOp",EDGE,"E6.bottom")])]})],"blendedInto":[makeQuery(id+"F1.opRevolve","SWEPT_FACE",FACE,{"disambiguationData":[OSD([sQuery(id+"F0.wireOp",EDGE,"E6.bottom")])]})]});
            fillet(context, id + "F11", {"entities" : qUnion([Q0, Q1]), "radius" : 0.5 * mm, "tangentPropagation" : true, "allowEdgeOverflow" : false});
        }
    });
